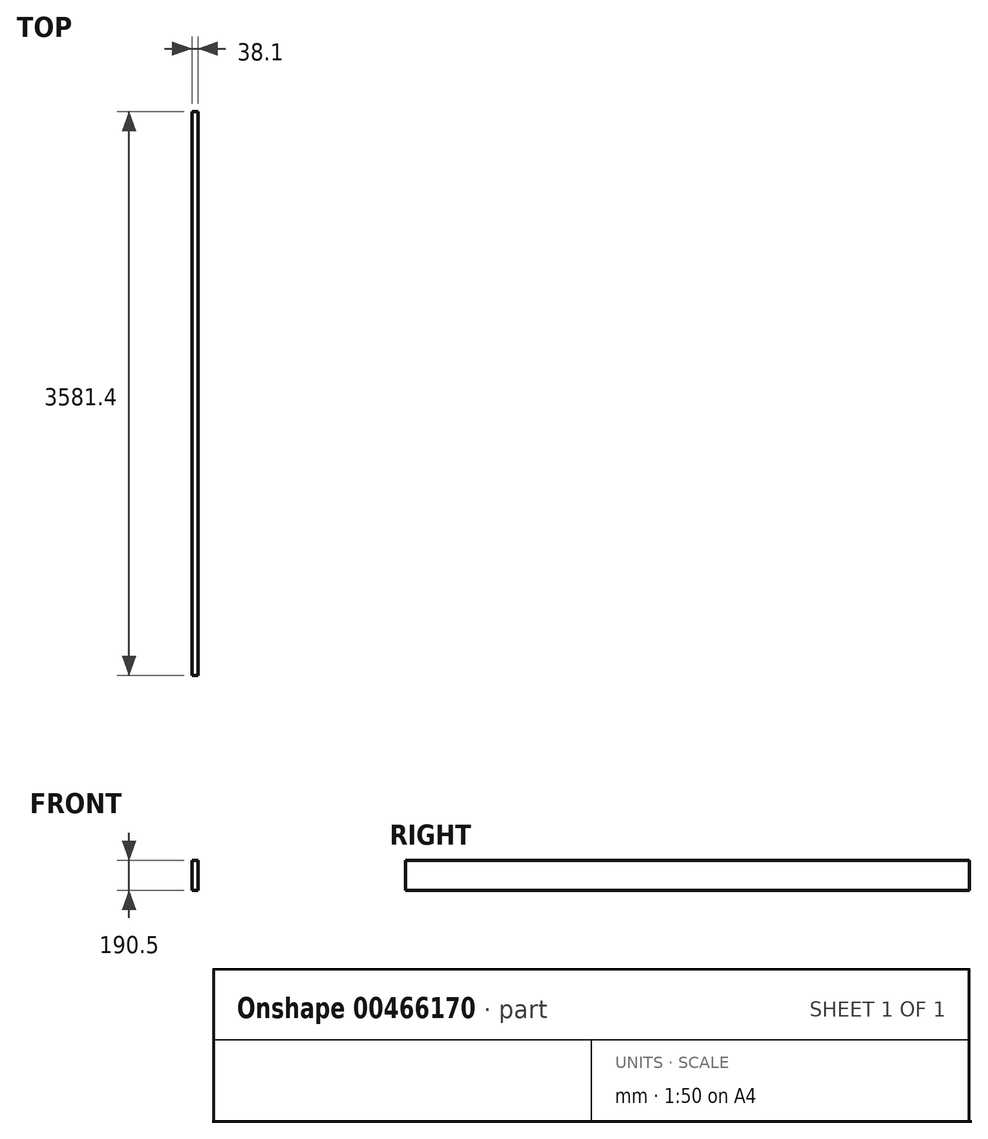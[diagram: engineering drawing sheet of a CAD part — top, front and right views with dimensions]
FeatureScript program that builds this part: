
annotation { "Feature Type Name" : "Feature", "Feature Type Description" : "" }
export const myFeature = defineFeature(function(context is Context, id is Id, definition is map)
    precondition{}
    {
        {
            var Q0;
            Q0=qCreatedBy(makeId("Front.planeOp"),FACE);
            var sketch = newSketch(context, id + "F0", { "sketchPlane" : qUnion([Q0])});
            skLineSegment(sketch, "E0.bottom", {"start": v(0, 0) * mm, "end": v(38.1, 0) * mm});
            skLineSegment(sketch, "E0.top", {"start": v(0, 190.5) * mm, "end": v(38.1, 190.5) * mm});
            skLineSegment(sketch, "E0.left", {"start": v(0, 0) * mm, "end": v(0, 190.5) * mm});
            skLineSegment(sketch, "E0.right", {"start": v(38.1, 0) * mm, "end": v(38.1, 190.5) * mm});
            skSolve(sketch);
        }
        {
            var Q0;
            Q0=makeQuery(id+"F0.imprint","IMPRINT",FACE,{"disambiguationData":[TD([[makeQuery(id+"F0.imprint","IMPRINT",EDGE,{"derivedFrom":sQuery(id+"F0.wireOp",EDGE,"E0.bottom")}),1.0]])]});
            extrude(context, id + "F1", {"entities" : qUnion([Q0]), "oppositeDirection" : true, "depth" : 3581.4 * mm});
        }
    });
